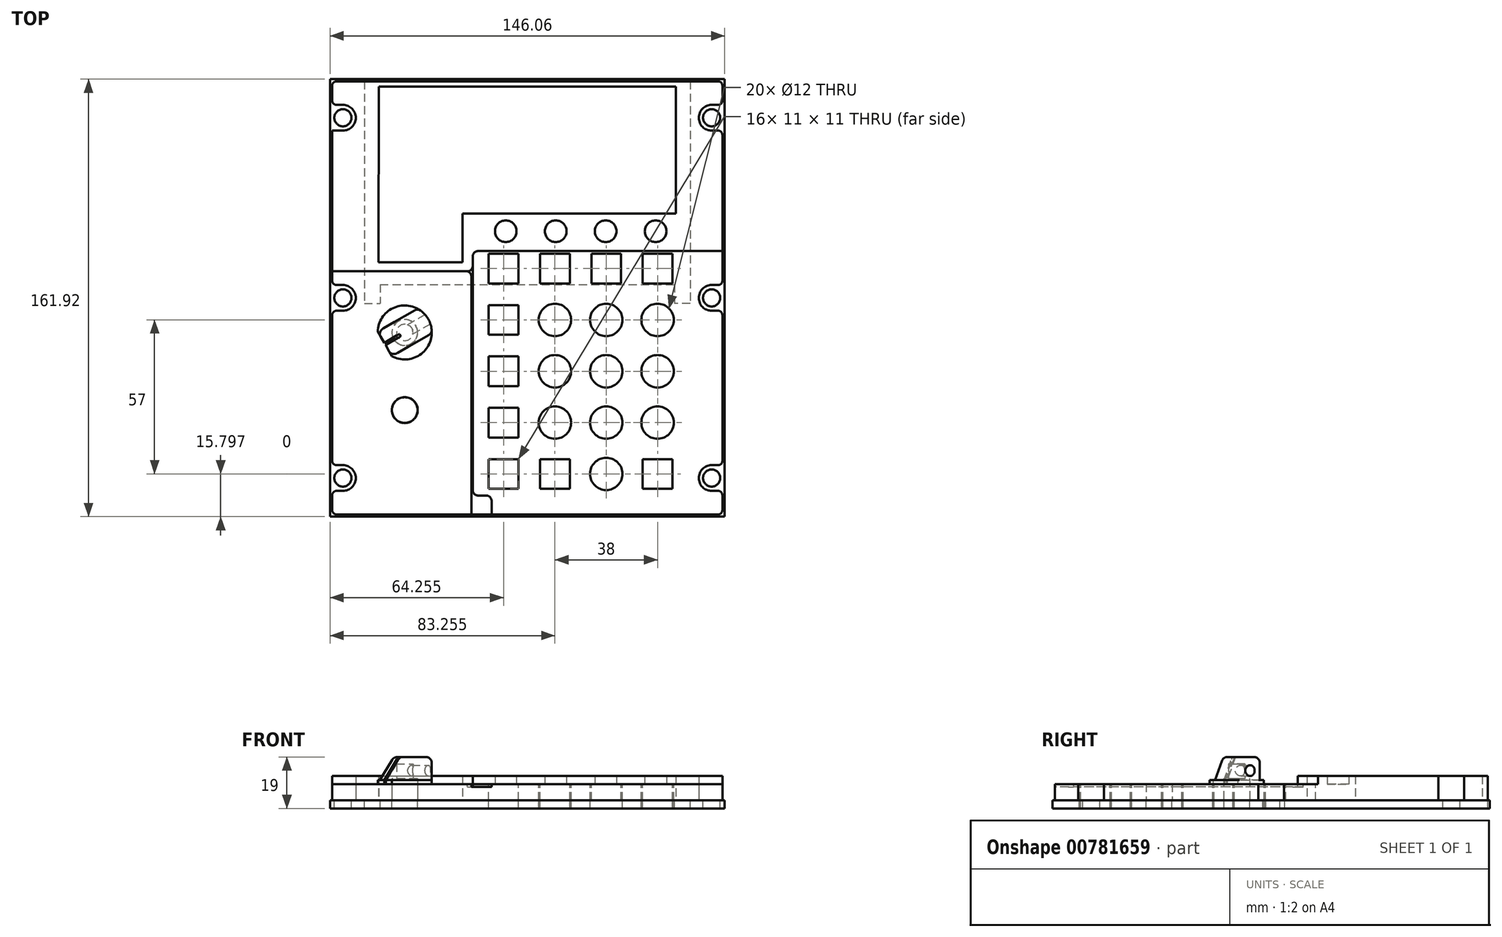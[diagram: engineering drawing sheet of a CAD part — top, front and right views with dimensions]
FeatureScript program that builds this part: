
annotation { "Feature Type Name" : "Feature", "Feature Type Description" : "" }
export const myFeature = defineFeature(function(context is Context, id is Id, definition is map)
    precondition{}
    {
        {
            var Q0;
            Q0=qCreatedBy(makeId("Top.planeOp"),FACE);
            var sketch = newSketch(context, id + "F0", { "sketchPlane" : qUnion([Q0])});
            skLineSegment(sketch, "E0.bottom", {"start": v(73.03, 80.96) * mm, "end": v(-73.03, 80.96) * mm});
            skLineSegment(sketch, "E0.top", {"start": v(73.02, -80.96) * mm, "end": v(-73.02, -80.96) * mm});
            skLineSegment(sketch, "E0.left", {"start": v(73.02, 80.96) * mm, "end": v(73.03, -80.96) * mm});
            skLineSegment(sketch, "E0.right", {"start": v(-73.03, 80.96) * mm, "end": v(-73.03, -80.96) * mm});
            skPoint(sketch, "E0.middle", {"position": v(0, 0) * mm});
            skLineSegment(sketch, "E1.bottom", {"start": v(-72.23, 80.16) * mm, "end": v(72.22, 80.16) * mm});
            skLineSegment(sketch, "E1.top", {"start": v(-72.23, -80.16) * mm, "end": v(72.22, -80.16) * mm});
            skLineSegment(sketch, "E1.left", {"start": v(-72.22, 80.16) * mm, "end": v(-72.22, 71.44) * mm});
            skLineSegment(sketch, "E1.right", {"start": v(72.23, 80.16) * mm, "end": v(72.23, 71.44) * mm});
            skCircle(sketch, "E2", {"center": v(-68.26, 66.67) * mm, "radius": 3.17 * mm});
            skArc(sketch, "E3", {"start": v(-68.26, 61.91) * mm, "mid": v(-63.5, 66.67) * mm, "end": v(-68.26, 71.44) * mm});
            skLineSegment(sketch, "E4", {"start": v(-68.26, 71.44) * mm, "end": v(-72.22, 71.44) * mm});
            skLineSegment(sketch, "E5", {"start": v(-68.26, 61.91) * mm, "end": v(-72.22, 61.91) * mm});
            skArc(sketch, "E6", {"start": v(-68.26, -4.76) * mm, "mid": v(-63.5, 0) * mm, "end": v(-68.26, 4.76) * mm});
            skCircle(sketch, "E7", {"center": v(-68.26, 0) * mm, "radius": 3.17 * mm});
            skLineSegment(sketch, "E8", {"start": v(-68.26, 4.76) * mm, "end": v(-72.23, 4.76) * mm});
            skLineSegment(sketch, "E9", {"start": v(-68.26, -4.76) * mm, "end": v(-72.23, -4.76) * mm});
            skLineSegment(sketch, "E10.trimOffspring", {"start": v(-72.23, -4.76) * mm, "end": v(-72.23, -61.91) * mm});
            skLineSegment(sketch, "E11.trimOffspring", {"start": v(-72.22, 61.91) * mm, "end": v(-72.23, 4.76) * mm});
            skLineSegment(sketch, "E12.MirrorCS", {"start": v(-68.26, -71.44) * mm, "end": v(-72.22, -71.44) * mm});
            skLineSegment(sketch, "E13.MirrorCS", {"start": v(-68.26, -61.91) * mm, "end": v(-72.22, -61.91) * mm});
            skCircle(sketch, "E14.MirrorC", {"center": v(-68.26, -66.67) * mm, "radius": 3.17 * mm});
            skArc(sketch, "E15.MirrorCS", {"start": v(-68.26, -61.91) * mm, "mid": v(-63.5, -66.67) * mm, "end": v(-68.26, -71.44) * mm});
            skCircle(sketch, "E16.MirrorC", {"center": v(68.26, 66.67) * mm, "radius": 3.17 * mm});
            skLineSegment(sketch, "E17.MirrorCS", {"start": v(68.26, 71.44) * mm, "end": v(72.22, 71.44) * mm});
            skLineSegment(sketch, "E18.MirrorCS", {"start": v(68.26, 4.76) * mm, "end": v(72.23, 4.76) * mm});
            skLineSegment(sketch, "E19.MirrorCS", {"start": v(68.26, 61.91) * mm, "end": v(72.22, 61.91) * mm});
            skLineSegment(sketch, "E20.MirrorCS", {"start": v(68.26, -4.76) * mm, "end": v(72.23, -4.76) * mm});
            skCircle(sketch, "E21.MirrorC", {"center": v(68.26, -66.67) * mm, "radius": 3.17 * mm});
            skCircle(sketch, "E22.MirrorC", {"center": v(68.26, 0) * mm, "radius": 3.17 * mm});
            skLineSegment(sketch, "E23.MirrorCS", {"start": v(68.26, -61.91) * mm, "end": v(72.22, -61.91) * mm});
            skArc(sketch, "E24.MirrorCS", {"start": v(68.26, 61.91) * mm, "mid": v(63.5, 66.67) * mm, "end": v(68.26, 71.44) * mm});
            skArc(sketch, "E25.MirrorCS", {"start": v(68.26, -4.76) * mm, "mid": v(63.5, 0) * mm, "end": v(68.26, 4.76) * mm});
            skArc(sketch, "E26.MirrorCS", {"start": v(68.26, -61.91) * mm, "mid": v(63.5, -66.67) * mm, "end": v(68.26, -71.44) * mm});
            skLineSegment(sketch, "E27.MirrorCS", {"start": v(68.26, -71.44) * mm, "end": v(72.22, -71.44) * mm});
            skLineSegment(sketch, "E28", {"start": v(-55.1, 13.16) * mm, "end": v(-23.98, 13.16) * mm});
            skLineSegment(sketch, "E29", {"start": v(-23.98, 13.16) * mm, "end": v(-23.98, 31.16) * mm});
            skLineSegment(sketch, "E30", {"start": v(-23.98, 31.16) * mm, "end": v(55, 31.16) * mm});
            skLineSegment(sketch, "E31", {"start": v(55, 31.16) * mm, "end": v(55, 78.16) * mm});
            skLineSegment(sketch, "E32", {"start": v(55, 78.16) * mm, "end": v(-55, 78.16) * mm});
            skLineSegment(sketch, "E33", {"start": v(-55, 78.16) * mm, "end": v(-55.1, 13.16) * mm});
            skPoint(sketch, "E34", {"position": v(-68.26, 14.26) * mm});
            skPoint(sketch, "E35", {"position": v(-68.26, 56.91) * mm});
            skPoint(sketch, "E36.MirrorP", {"position": v(-68.26, -14.26) * mm});
            skPoint(sketch, "E37.MirrorP", {"position": v(-68.26, -56.91) * mm});
            skPoint(sketch, "E38.MirrorP", {"position": v(68.26, 14.26) * mm});
            skPoint(sketch, "E39.MirrorP", {"position": v(68.26, -14.26) * mm});
            skPoint(sketch, "E40.MirrorP", {"position": v(68.26, -56.91) * mm});
            skPoint(sketch, "E41.MirrorP", {"position": v(68.26, 56.91) * mm});
            skPoint(sketch, "E42", {"position": v(-45.37, -12.8) * mm});
            skPoint(sketch, "E43", {"position": v(-45.37, -41.53) * mm});
            skPoint(sketch, "E44", {"position": v(-45.37, -66.67) * mm});
            skLineSegment(sketch, "E45.trimOffspring", {"start": v(-72.23, -71.44) * mm, "end": v(-72.23, -80.16) * mm});
            skLineSegment(sketch, "E46.trimOffspring", {"start": v(72.22, -71.44) * mm, "end": v(72.22, -80.16) * mm});
            skLineSegment(sketch, "E47.trimOffspring", {"start": v(72.23, -4.76) * mm, "end": v(72.22, -61.91) * mm});
            skLineSegment(sketch, "E48.trimOffspring", {"start": v(72.23, 61.91) * mm, "end": v(72.23, 4.76) * mm});
            skSolve(sketch);
        }
        {
            var Q0;
            Q0=makeQuery(id+"F0.imprint","IMPRINT",FACE,{"disambiguationData":[TD([[makeQuery(id+"F0.imprint","IMPRINT",EDGE,{"derivedFrom":sQuery(id+"F0.wireOp",EDGE,"E0.bottom")}),1.0]])]});
            var Q1;
            {var subQ8=sQuery(id+"F0.wireOp",EDGE,"E1.bottom");Q1=makeQuery(id+"F0.imprint","IMPRINT",FACE,{"disambiguationData":[TD([[makeQuery(id+"F0.imprint","IMPRINT",EDGE,{"derivedFrom":subQ8}),-1.0]])]});}
            var Q2;
            Q2=makeQuery(id+"F0.imprint","IMPRINT",FACE,{"disambiguationData":[TD([[makeQuery(id+"F0.imprint","IMPRINT",EDGE,{"derivedFrom":sQuery(id+"F0.wireOp",EDGE,"E28")}),1.0]])]});
            extrude(context, id + "F1", {"entities" : qUnion([Q0, Q1, Q2]), "oppositeDirection" : true, "depth" : 3 * mm, "offsetDistance" : 25 * mm});
        }
        {
            var Q0;
            Q0=makeQuery(id+"F0.imprint","IMPRINT",FACE,{"disambiguationData":[TD([[makeQuery(id+"F0.imprint","IMPRINT",EDGE,{"derivedFrom":sQuery(id+"F0.wireOp",EDGE,"E1.bottom")}),-1.0]])]});
            extrude(context, id + "F2", {"entities" : qUnion([Q0]), "depth" : 6 * mm, "offsetDistance" : 25 * mm});
        }
        {
            var Q0;
            Q0=makeQuery(id+"F2.opExtrude","SWEPT_EDGE",EDGE,{"disambiguationData":[OSD([sQuery(id+"F0.wireOp",EDGE,"E1.top"),sQuery(id+"F0.wireOp",EDGE,"E45.trimOffspring")])]});
            var Q1;
            Q1=makeQuery(id+"F2.opExtrude","SWEPT_EDGE",EDGE,{"disambiguationData":[OSD([sQuery(id+"F0.wireOp",EDGE,"E10.trimOffspring"),sQuery(id+"F0.wireOp",EDGE,"E13.MirrorCS")])]});
            var Q2;
            Q2=makeQuery(id+"F2.opExtrude","SWEPT_EDGE",EDGE,{"disambiguationData":[OSD([sQuery(id+"F0.wireOp",EDGE,"E12.MirrorCS"),sQuery(id+"F0.wireOp",EDGE,"E45.trimOffspring")])]});
            var Q3;
            Q3=makeQuery(id+"F2.opExtrude","SWEPT_EDGE",EDGE,{"disambiguationData":[OSD([sQuery(id+"F0.wireOp",EDGE,"E9"),sQuery(id+"F0.wireOp",EDGE,"E10.trimOffspring")])]});
            var Q4;
            Q4=makeQuery(id+"F2.opExtrude","SWEPT_EDGE",EDGE,{"disambiguationData":[OSD([sQuery(id+"F0.wireOp",EDGE,"E8"),sQuery(id+"F0.wireOp",EDGE,"E11.trimOffspring")])]});
            var Q5;
            Q5=makeQuery(id+"F2.opExtrude","SWEPT_EDGE",EDGE,{"disambiguationData":[OSD([sQuery(id+"F0.wireOp",EDGE,"E1.bottom"),sQuery(id+"F0.wireOp",EDGE,"E1.left")])]});
            var Q6;
            Q6=makeQuery(id+"F2.opExtrude","SWEPT_EDGE",EDGE,{"disambiguationData":[OSD([sQuery(id+"F0.wireOp",EDGE,"E1.left"),sQuery(id+"F0.wireOp",EDGE,"E4")])]});
            var Q7;
            Q7=makeQuery(id+"F2.opExtrude","SWEPT_EDGE",EDGE,{"disambiguationData":[OSD([sQuery(id+"F0.wireOp",EDGE,"E1.top"),sQuery(id+"F0.wireOp",EDGE,"E46.trimOffspring")])]});
            var Q8;
            Q8=makeQuery(id+"F2.opExtrude","SWEPT_EDGE",EDGE,{"disambiguationData":[OSD([sQuery(id+"F0.wireOp",EDGE,"E27.MirrorCS"),sQuery(id+"F0.wireOp",EDGE,"E46.trimOffspring")])]});
            var Q9;
            Q9=makeQuery(id+"F2.opExtrude","SWEPT_EDGE",EDGE,{"disambiguationData":[OSD([sQuery(id+"F0.wireOp",EDGE,"E23.MirrorCS"),sQuery(id+"F0.wireOp",EDGE,"E47.trimOffspring")])]});
            var Q10;
            Q10=makeQuery(id+"F2.opExtrude","SWEPT_EDGE",EDGE,{"disambiguationData":[OSD([sQuery(id+"F0.wireOp",EDGE,"E20.MirrorCS"),sQuery(id+"F0.wireOp",EDGE,"E47.trimOffspring")])]});
            var Q11;
            Q11=makeQuery(id+"F2.opExtrude","SWEPT_EDGE",EDGE,{"disambiguationData":[OSD([sQuery(id+"F0.wireOp",EDGE,"E18.MirrorCS"),sQuery(id+"F0.wireOp",EDGE,"E48.trimOffspring")])]});
            var Q12;
            Q12=makeQuery(id+"F2.opExtrude","SWEPT_EDGE",EDGE,{"disambiguationData":[OSD([sQuery(id+"F0.wireOp",EDGE,"E1.right"),sQuery(id+"F0.wireOp",EDGE,"E17.MirrorCS")])]});
            var Q13;
            Q13=makeQuery(id+"F2.opExtrude","SWEPT_EDGE",EDGE,{"disambiguationData":[OSD([sQuery(id+"F0.wireOp",EDGE,"E19.MirrorCS"),sQuery(id+"F0.wireOp",EDGE,"E48.trimOffspring")])]});
            var Q14;
            Q14=makeQuery(id+"F2.opExtrude","SWEPT_EDGE",EDGE,{"disambiguationData":[OSD([sQuery(id+"F0.wireOp",EDGE,"E1.bottom"),sQuery(id+"F0.wireOp",EDGE,"E1.right")])]});
            fillet(context, id + "F3", {"entities" : qUnion([Q0, Q1, Q2, Q3, Q4, Q5, Q6, Q7, Q8, Q9, Q10, Q11, Q12, Q13, Q14]), "radius" : 1.59 * mm, "tangentPropagation" : true, "allowEdgeOverflow" : false});
        }
        {
            var Q0;
            Q0=makeQuery(id+"F0.imprint","IMPRINT",FACE,{"disambiguationData":[TD([[makeQuery(id+"F0.imprint","IMPRINT",EDGE,{"derivedFrom":sQuery(id+"F0.wireOp",EDGE,"E1.bottom")}),-1.0]])]});
            var sketch = newSketch(context, id + "F4", { "sketchPlane" : qUnion([Q0])});
            skLineSegment(sketch, "E49.bottom", {"start": v(54, 77.6) * mm, "end": v(-54, 77.6) * mm});
            skLineSegment(sketch, "E49.top", {"start": v(54, 12.8) * mm, "end": v(-54, 12.8) * mm});
            skLineSegment(sketch, "E49.left", {"start": v(54, 77.6) * mm, "end": v(54, 12.8) * mm});
            skLineSegment(sketch, "E49.right", {"start": v(-54, 77.6) * mm, "end": v(-54, 12.8) * mm});
            skPoint(sketch, "E49.middle", {"position": v(0, 42.96) * mm});
            skLineSegment(sketch, "E50.bottom", {"start": v(-60.35, 80.96) * mm, "end": v(60.35, 80.96) * mm});
            skLineSegment(sketch, "E50.top", {"start": v(-54.5, 4.96) * mm, "end": v(54.5, 4.96) * mm});
            skLineSegment(sketch, "E50.left", {"start": v(-60.35, 80.96) * mm, "end": v(-60.35, 4.96) * mm});
            skLineSegment(sketch, "E50.right", {"start": v(60.35, 80.96) * mm, "end": v(60.35, 4.96) * mm});
            skLineSegment(sketch, "E51.top", {"start": v(-60.35, -2.04) * mm, "end": v(-54.5, -2.04) * mm});
            skLineSegment(sketch, "E51.left", {"start": v(-60.35, 4.96) * mm, "end": v(-60.35, -2.04) * mm});
            skLineSegment(sketch, "E51.right", {"start": v(-54.5, 4.96) * mm, "end": v(-54.5, -2.04) * mm});
            skLineSegment(sketch, "E52.MirrorCS", {"start": v(60.35, 4.96) * mm, "end": v(60.35, -2.04) * mm});
            skLineSegment(sketch, "E53.MirrorCS", {"start": v(60.35, -2.04) * mm, "end": v(54.5, -2.04) * mm});
            skLineSegment(sketch, "E54.MirrorCS", {"start": v(54.5, 4.96) * mm, "end": v(54.5, -2.04) * mm});
            skLineSegment(sketch, "E55", {"start": v(-54.5, 4.96) * mm, "end": v(-60.35, 4.96) * mm});
            skLineSegment(sketch, "E56", {"start": v(54.5, 4.96) * mm, "end": v(60.35, 4.96) * mm});
            skSolve(sketch);
        }
        {
            var Q0;
            Q0=makeQuery(id+"F2.opExtrude","CAP_FACE",FACE,{"disambiguationData":[OSD([sQuery(id+"F0.wireOp",EDGE,"E1.bottom"),sQuery(id+"F0.wireOp",EDGE,"E1.top"),sQuery(id+"F0.wireOp",EDGE,"E1.left"),sQuery(id+"F0.wireOp",EDGE,"E1.right"),sQuery(id+"F0.wireOp",EDGE,"E3"),sQuery(id+"F0.wireOp",EDGE,"E4"),sQuery(id+"F0.wireOp",EDGE,"E5"),sQuery(id+"F0.wireOp",EDGE,"E6"),sQuery(id+"F0.wireOp",EDGE,"E8"),sQuery(id+"F0.wireOp",EDGE,"E9"),sQuery(id+"F0.wireOp",EDGE,"E10.trimOffspring"),sQuery(id+"F0.wireOp",EDGE,"E11.trimOffspring"),sQuery(id+"F0.wireOp",EDGE,"E12.MirrorCS"),sQuery(id+"F0.wireOp",EDGE,"E13.MirrorCS"),sQuery(id+"F0.wireOp",EDGE,"E15.MirrorCS"),sQuery(id+"F0.wireOp",EDGE,"E17.MirrorCS"),sQuery(id+"F0.wireOp",EDGE,"E18.MirrorCS"),sQuery(id+"F0.wireOp",EDGE,"E19.MirrorCS"),sQuery(id+"F0.wireOp",EDGE,"E20.MirrorCS"),sQuery(id+"F0.wireOp",EDGE,"E23.MirrorCS"),sQuery(id+"F0.wireOp",EDGE,"E24.MirrorCS"),sQuery(id+"F0.wireOp",EDGE,"E25.MirrorCS"),sQuery(id+"F0.wireOp",EDGE,"E26.MirrorCS"),sQuery(id+"F0.wireOp",EDGE,"E27.MirrorCS"),sQuery(id+"F0.wireOp",EDGE,"E28"),sQuery(id+"F0.wireOp",EDGE,"E29"),sQuery(id+"F0.wireOp",EDGE,"E30"),sQuery(id+"F0.wireOp",EDGE,"E31"),sQuery(id+"F0.wireOp",EDGE,"E32"),sQuery(id+"F0.wireOp",EDGE,"E33"),sQuery(id+"F0.wireOp",EDGE,"E45.trimOffspring"),sQuery(id+"F0.wireOp",EDGE,"E46.trimOffspring"),sQuery(id+"F0.wireOp",EDGE,"E47.trimOffspring"),sQuery(id+"F0.wireOp",EDGE,"E48.trimOffspring")])],"isStart":false});
            var sketch = newSketch(context, id + "F5", { "sketchPlane" : qUnion([Q0])});
            skCircle(sketch, "E57", {"center": v(10.23, -8.16) * mm, "radius": 6 * mm});
            skCircle(sketch, "E58.0.1.0", {"center": v(10.23, -27.16) * mm, "radius": 6 * mm});
            skCircle(sketch, "E58.0.2.0", {"center": v(10.23, -46.16) * mm, "radius": 6 * mm});
            skCircle(sketch, "E58.1.0.0", {"center": v(29.23, -8.16) * mm, "radius": 6 * mm});
            skCircle(sketch, "E58.1.1.0", {"center": v(29.23, -27.16) * mm, "radius": 6 * mm});
            skCircle(sketch, "E58.1.2.0", {"center": v(29.23, -46.16) * mm, "radius": 6 * mm});
            skCircle(sketch, "E58.2.0.0", {"center": v(48.23, -8.16) * mm, "radius": 6 * mm});
            skCircle(sketch, "E58.2.1.0", {"center": v(48.23, -27.16) * mm, "radius": 6 * mm});
            skCircle(sketch, "E58.2.2.0", {"center": v(48.23, -46.16) * mm, "radius": 6 * mm});
            skLineSegment(sketch, "E58.direction1", {"start": v(10.23, -8.16) * mm, "end": v(29.23, -8.16) * mm, "construction": true});
            skLineSegment(sketch, "E58.direction2", {"start": v(10.23, -8.16) * mm, "end": v(10.23, -27.16) * mm, "construction": true});
            skCircle(sketch, "E59", {"center": v(29.23, -65.16) * mm, "radius": 6 * mm});
            skLineSegment(sketch, "E60.bottom", {"start": v(15.73, 16.34) * mm, "end": v(4.73, 16.34) * mm});
            skLineSegment(sketch, "E60.top", {"start": v(15.73, 5.34) * mm, "end": v(4.73, 5.34) * mm});
            skLineSegment(sketch, "E60.left", {"start": v(15.73, 16.34) * mm, "end": v(15.73, 5.34) * mm});
            skLineSegment(sketch, "E60.right", {"start": v(4.73, 16.34) * mm, "end": v(4.73, 5.34) * mm});
            skPoint(sketch, "E60.middle", {"position": v(10.23, 10.84) * mm});
            skLineSegment(sketch, "E61.1.0.0", {"start": v(34.73, 16.34) * mm, "end": v(23.73, 16.34) * mm});
            skLineSegment(sketch, "E61.1.0.1", {"start": v(34.73, 5.34) * mm, "end": v(23.73, 5.34) * mm});
            skLineSegment(sketch, "E61.1.0.2", {"start": v(34.73, 16.34) * mm, "end": v(34.73, 5.34) * mm});
            skLineSegment(sketch, "E61.1.0.3", {"start": v(23.73, 16.34) * mm, "end": v(23.73, 5.34) * mm});
            skPoint(sketch, "E61.1.0.4", {"position": v(29.23, 10.84) * mm});
            skLineSegment(sketch, "E61.2.0.0", {"start": v(53.73, 16.34) * mm, "end": v(42.73, 16.34) * mm});
            skLineSegment(sketch, "E61.2.0.1", {"start": v(53.73, 5.34) * mm, "end": v(42.73, 5.34) * mm});
            skLineSegment(sketch, "E61.2.0.2", {"start": v(53.73, 16.34) * mm, "end": v(53.73, 5.34) * mm});
            skLineSegment(sketch, "E61.2.0.3", {"start": v(42.73, 16.34) * mm, "end": v(42.73, 5.34) * mm});
            skPoint(sketch, "E61.2.0.4", {"position": v(48.23, 10.84) * mm});
            skLineSegment(sketch, "E61.direction1", {"start": v(4.73, 5.34) * mm, "end": v(23.73, 5.34) * mm, "construction": true});
            skLineSegment(sketch, "E62.bottom", {"start": v(-3.27, 16.34) * mm, "end": v(-14.27, 16.34) * mm});
            skLineSegment(sketch, "E62.top", {"start": v(-3.27, 5.34) * mm, "end": v(-14.27, 5.34) * mm});
            skLineSegment(sketch, "E62.left", {"start": v(-3.27, 16.34) * mm, "end": v(-3.27, 5.34) * mm});
            skLineSegment(sketch, "E62.right", {"start": v(-14.27, 16.34) * mm, "end": v(-14.27, 5.34) * mm});
            skPoint(sketch, "E62.middle", {"position": v(-8.77, 10.84) * mm});
            skLineSegment(sketch, "E63.bottom", {"start": v(-3.27, -2.66) * mm, "end": v(-14.27, -2.66) * mm});
            skLineSegment(sketch, "E63.top", {"start": v(-3.27, -13.66) * mm, "end": v(-14.27, -13.66) * mm});
            skLineSegment(sketch, "E63.left", {"start": v(-3.27, -2.66) * mm, "end": v(-3.27, -13.66) * mm});
            skLineSegment(sketch, "E63.right", {"start": v(-14.27, -2.66) * mm, "end": v(-14.27, -13.66) * mm});
            skPoint(sketch, "E63.middle", {"position": v(-8.77, -8.16) * mm});
            skPoint(sketch, "E63.middle.positionSnap0", {"position": v(-8.77, 5.34) * mm});
            skPoint(sketch, "E63.centerSnap0", {"position": v(-8.77, 5.34) * mm});
            skLineSegment(sketch, "E64.bottom", {"start": v(-3.27, -21.66) * mm, "end": v(-14.28, -21.66) * mm});
            skLineSegment(sketch, "E64.top", {"start": v(-3.27, -32.66) * mm, "end": v(-14.27, -32.66) * mm});
            skLineSegment(sketch, "E64.left", {"start": v(-3.27, -21.66) * mm, "end": v(-3.27, -32.66) * mm});
            skLineSegment(sketch, "E64.right", {"start": v(-14.27, -21.66) * mm, "end": v(-14.27, -32.66) * mm});
            skPoint(sketch, "E64.middle", {"position": v(-8.77, -27.16) * mm});
            skLineSegment(sketch, "E65.bottom", {"start": v(-3.27, -40.66) * mm, "end": v(-14.27, -40.66) * mm});
            skLineSegment(sketch, "E65.top", {"start": v(-3.27, -51.66) * mm, "end": v(-14.27, -51.66) * mm});
            skLineSegment(sketch, "E65.left", {"start": v(-3.27, -40.66) * mm, "end": v(-3.27, -51.66) * mm});
            skLineSegment(sketch, "E65.right", {"start": v(-14.27, -40.66) * mm, "end": v(-14.27, -51.66) * mm});
            skPoint(sketch, "E65.middle", {"position": v(-8.77, -46.16) * mm});
            skLineSegment(sketch, "E66.bottom", {"start": v(-3.27, -59.66) * mm, "end": v(-14.27, -59.66) * mm});
            skLineSegment(sketch, "E66.top", {"start": v(-3.27, -70.66) * mm, "end": v(-14.27, -70.66) * mm});
            skLineSegment(sketch, "E66.left", {"start": v(-3.27, -59.66) * mm, "end": v(-3.27, -70.66) * mm});
            skLineSegment(sketch, "E66.right", {"start": v(-14.27, -59.66) * mm, "end": v(-14.27, -70.66) * mm});
            skPoint(sketch, "E66.middle", {"position": v(-8.77, -65.16) * mm});
            skLineSegment(sketch, "E67.bottom", {"start": v(15.73, -59.66) * mm, "end": v(4.73, -59.66) * mm});
            skLineSegment(sketch, "E67.top", {"start": v(15.73, -70.66) * mm, "end": v(4.73, -70.66) * mm});
            skLineSegment(sketch, "E67.left", {"start": v(15.73, -59.66) * mm, "end": v(15.73, -70.66) * mm});
            skLineSegment(sketch, "E67.right", {"start": v(4.73, -59.66) * mm, "end": v(4.73, -70.66) * mm});
            skPoint(sketch, "E67.middle", {"position": v(10.23, -65.16) * mm});
            skLineSegment(sketch, "E68.bottom", {"start": v(53.72, -59.66) * mm, "end": v(42.73, -59.66) * mm});
            skLineSegment(sketch, "E68.top", {"start": v(53.72, -70.66) * mm, "end": v(42.73, -70.66) * mm});
            skLineSegment(sketch, "E68.left", {"start": v(53.72, -59.66) * mm, "end": v(53.72, -70.66) * mm});
            skLineSegment(sketch, "E68.right", {"start": v(42.73, -59.66) * mm, "end": v(42.73, -70.66) * mm});
            skPoint(sketch, "E68.middle", {"position": v(48.23, -65.16) * mm});
            skSolve(sketch);
        }
        {
            var Q0;
            Q0 = qSketchRegion(id + "F5", true);
            extrude(context, id + "F6", {"entities" : qUnion([Q0]), "operationType" : NewBodyOperationType.REMOVE, "oppositeDirection" : true, "depth" : 25 * mm, "offsetDistance" : 25 * mm});
        }
        {
            var Q0;
            Q0=sQuery(id+"F0.wireOp",VERTEX,"E42");
            var Q1;
            Q1=sQuery(id+"F0.wireOp",VERTEX,"E43");
            var Q2;
            Q2=makeQuery(id+"F1.opExtrude","SWEPT_BODY",BODY,{"disambiguationData":[OSD([sQuery(id+"F0.wireOp",EDGE,"E0.bottom"),sQuery(id+"F0.wireOp",EDGE,"E0.top"),sQuery(id+"F0.wireOp",EDGE,"E0.left"),sQuery(id+"F0.wireOp",EDGE,"E0.right"),sQuery(id+"F0.wireOp",EDGE,"E2"),sQuery(id+"F0.wireOp",EDGE,"E7"),sQuery(id+"F0.wireOp",EDGE,"E14.MirrorC"),sQuery(id+"F0.wireOp",EDGE,"E16.MirrorC"),sQuery(id+"F0.wireOp",EDGE,"E21.MirrorC"),sQuery(id+"F0.wireOp",EDGE,"E22.MirrorC")])]});
            hole(context, id + "F7", {"style" : HoleStyle.SIMPLE, "endStyle" : HoleEndStyle.BLIND, "holeDiameter" : 9.5 * mm, "majorDiameter" : 5 * mm, "holeDepth" : 25 * mm, "isTappedThrough" : true, "tappedDepth" : 12 * mm, "tapClearance" : 3, "locations" : qUnion([Q0, Q1]), "scope" : qUnion([Q2])});
        }
        {
            var Q0;
            Q0=sQuery(id+"F0.wireOp",VERTEX,"E42");
            var Q1;
            Q1=sQuery(id+"F0.wireOp",VERTEX,"E43");
            var Q2;
            Q2=makeQuery(id+"F2.opExtrude","SWEPT_BODY",BODY,{"disambiguationData":[OSD([sQuery(id+"F0.wireOp",EDGE,"E1.bottom"),sQuery(id+"F0.wireOp",EDGE,"E1.top"),sQuery(id+"F0.wireOp",EDGE,"E1.left"),sQuery(id+"F0.wireOp",EDGE,"E1.right"),sQuery(id+"F0.wireOp",EDGE,"E3"),sQuery(id+"F0.wireOp",EDGE,"E4"),sQuery(id+"F0.wireOp",EDGE,"E5"),sQuery(id+"F0.wireOp",EDGE,"E6"),sQuery(id+"F0.wireOp",EDGE,"E8"),sQuery(id+"F0.wireOp",EDGE,"E9"),sQuery(id+"F0.wireOp",EDGE,"E10.trimOffspring"),sQuery(id+"F0.wireOp",EDGE,"E11.trimOffspring"),sQuery(id+"F0.wireOp",EDGE,"E12.MirrorCS"),sQuery(id+"F0.wireOp",EDGE,"E13.MirrorCS"),sQuery(id+"F0.wireOp",EDGE,"E15.MirrorCS"),sQuery(id+"F0.wireOp",EDGE,"E17.MirrorCS"),sQuery(id+"F0.wireOp",EDGE,"E18.MirrorCS"),sQuery(id+"F0.wireOp",EDGE,"E19.MirrorCS"),sQuery(id+"F0.wireOp",EDGE,"E20.MirrorCS"),sQuery(id+"F0.wireOp",EDGE,"E23.MirrorCS"),sQuery(id+"F0.wireOp",EDGE,"E24.MirrorCS"),sQuery(id+"F0.wireOp",EDGE,"E25.MirrorCS"),sQuery(id+"F0.wireOp",EDGE,"E26.MirrorCS"),sQuery(id+"F0.wireOp",EDGE,"E27.MirrorCS"),sQuery(id+"F0.wireOp",EDGE,"E28"),sQuery(id+"F0.wireOp",EDGE,"E29"),sQuery(id+"F0.wireOp",EDGE,"E30"),sQuery(id+"F0.wireOp",EDGE,"E31"),sQuery(id+"F0.wireOp",EDGE,"E32"),sQuery(id+"F0.wireOp",EDGE,"E33"),sQuery(id+"F0.wireOp",EDGE,"E45.trimOffspring"),sQuery(id+"F0.wireOp",EDGE,"E46.trimOffspring"),sQuery(id+"F0.wireOp",EDGE,"E47.trimOffspring"),sQuery(id+"F0.wireOp",EDGE,"E48.trimOffspring")])]});
            hole(context, id + "F8", {"style" : HoleStyle.SIMPLE, "endStyle" : HoleEndStyle.BLIND, "oppositeDirection" : true, "holeDiameter" : 9.6 * mm, "majorDiameter" : 5 * mm, "holeDepth" : 25 * mm, "isTappedThrough" : true, "tappedDepth" : 12 * mm, "tapClearance" : 3, "locations" : qUnion([Q0, Q1]), "scope" : qUnion([Q2])});
        }
        {
            var Q0;
            Q0=makeQuery(id+"F2.opExtrude","CAP_FACE",FACE,{"disambiguationData":[OSD([sQuery(id+"F0.wireOp",EDGE,"E1.bottom"),sQuery(id+"F0.wireOp",EDGE,"E1.top"),sQuery(id+"F0.wireOp",EDGE,"E1.left"),sQuery(id+"F0.wireOp",EDGE,"E1.right"),sQuery(id+"F0.wireOp",EDGE,"E3"),sQuery(id+"F0.wireOp",EDGE,"E4"),sQuery(id+"F0.wireOp",EDGE,"E5"),sQuery(id+"F0.wireOp",EDGE,"E6"),sQuery(id+"F0.wireOp",EDGE,"E8"),sQuery(id+"F0.wireOp",EDGE,"E9"),sQuery(id+"F0.wireOp",EDGE,"E10.trimOffspring"),sQuery(id+"F0.wireOp",EDGE,"E11.trimOffspring"),sQuery(id+"F0.wireOp",EDGE,"E12.MirrorCS"),sQuery(id+"F0.wireOp",EDGE,"E13.MirrorCS"),sQuery(id+"F0.wireOp",EDGE,"E15.MirrorCS"),sQuery(id+"F0.wireOp",EDGE,"E17.MirrorCS"),sQuery(id+"F0.wireOp",EDGE,"E18.MirrorCS"),sQuery(id+"F0.wireOp",EDGE,"E19.MirrorCS"),sQuery(id+"F0.wireOp",EDGE,"E20.MirrorCS"),sQuery(id+"F0.wireOp",EDGE,"E23.MirrorCS"),sQuery(id+"F0.wireOp",EDGE,"E24.MirrorCS"),sQuery(id+"F0.wireOp",EDGE,"E25.MirrorCS"),sQuery(id+"F0.wireOp",EDGE,"E26.MirrorCS"),sQuery(id+"F0.wireOp",EDGE,"E27.MirrorCS"),sQuery(id+"F0.wireOp",EDGE,"E28"),sQuery(id+"F0.wireOp",EDGE,"E29"),sQuery(id+"F0.wireOp",EDGE,"E30"),sQuery(id+"F0.wireOp",EDGE,"E31"),sQuery(id+"F0.wireOp",EDGE,"E32"),sQuery(id+"F0.wireOp",EDGE,"E33"),sQuery(id+"F0.wireOp",EDGE,"E45.trimOffspring"),sQuery(id+"F0.wireOp",EDGE,"E46.trimOffspring"),sQuery(id+"F0.wireOp",EDGE,"E47.trimOffspring"),sQuery(id+"F0.wireOp",EDGE,"E48.trimOffspring")])],"isStart":false});
            var sketch = newSketch(context, id + "F9", { "sketchPlane" : qUnion([Q0])});
            skArc(sketch, "E69", {"start": v(-50.1, -21.6) * mm, "mid": v(-36.71, -7.8) * mm, "end": v(-55.37, -12.49) * mm});
            skLineSegment(sketch, "E70", {"start": v(-50.1, -21.6) * mm, "end": v(-55.37, -12.49) * mm});
            skLineSegment(sketch, "E71", {"start": v(-55.37, -12.49) * mm, "end": v(-40.65, -3.99) * mm});
            skLineSegment(sketch, "E72", {"start": v(-50.1, -21.6) * mm, "end": v(-35.38, -13.1) * mm});
            skLineSegment(sketch, "E73", {"start": v(-44.9, -18.6) * mm, "end": v(-50.17, -9.49) * mm});
            skSolve(sketch);
        }
        {
            var Q0;
            {var subQ5=sQuery(id+"F9.wireOp",EDGE,"E69");var subQ7=sQuery(id+"F9.wireOp",EDGE,"E71");var subQ8=makeQuery(id+"F9.imprint","INTERSECT",VERTEX,{"derivedFrom":[subQ5,subQ7]});Q0=makeQuery(id+"F9.imprint","IMPRINT",FACE,{"disambiguationData":[TD([[makeQuery(id+"F9.imprint","IMPRINT",EDGE,{"disambiguationData":[TD([[subQ8,1.0]])],"derivedFrom":subQ5}),1.0]])]});}
            var Q1;
            {var subQ0=sQuery(id+"F9.wireOp",EDGE,"E73");var subQ1=makeQuery(id+"F8.hole-0.boolean.opBoolean","INTERSECT",EDGE,{"derivedFrom":[makeQuery(id+"F2.opExtrude","CAP_FACE",FACE,{"disambiguationData":[OSD([sQuery(id+"F0.wireOp",EDGE,"E1.bottom"),sQuery(id+"F0.wireOp",EDGE,"E1.top"),sQuery(id+"F0.wireOp",EDGE,"E1.left"),sQuery(id+"F0.wireOp",EDGE,"E1.right"),sQuery(id+"F0.wireOp",EDGE,"E3"),sQuery(id+"F0.wireOp",EDGE,"E4"),sQuery(id+"F0.wireOp",EDGE,"E5"),sQuery(id+"F0.wireOp",EDGE,"E6"),sQuery(id+"F0.wireOp",EDGE,"E8"),sQuery(id+"F0.wireOp",EDGE,"E9"),sQuery(id+"F0.wireOp",EDGE,"E10.trimOffspring"),sQuery(id+"F0.wireOp",EDGE,"E11.trimOffspring"),sQuery(id+"F0.wireOp",EDGE,"E12.MirrorCS"),sQuery(id+"F0.wireOp",EDGE,"E13.MirrorCS"),sQuery(id+"F0.wireOp",EDGE,"E15.MirrorCS"),sQuery(id+"F0.wireOp",EDGE,"E17.MirrorCS"),sQuery(id+"F0.wireOp",EDGE,"E18.MirrorCS"),sQuery(id+"F0.wireOp",EDGE,"E19.MirrorCS"),sQuery(id+"F0.wireOp",EDGE,"E20.MirrorCS"),sQuery(id+"F0.wireOp",EDGE,"E23.MirrorCS"),sQuery(id+"F0.wireOp",EDGE,"E24.MirrorCS"),sQuery(id+"F0.wireOp",EDGE,"E25.MirrorCS"),sQuery(id+"F0.wireOp",EDGE,"E26.MirrorCS"),sQuery(id+"F0.wireOp",EDGE,"E27.MirrorCS"),sQuery(id+"F0.wireOp",EDGE,"E28"),sQuery(id+"F0.wireOp",EDGE,"E29"),sQuery(id+"F0.wireOp",EDGE,"E30"),sQuery(id+"F0.wireOp",EDGE,"E31"),sQuery(id+"F0.wireOp",EDGE,"E32"),sQuery(id+"F0.wireOp",EDGE,"E33"),sQuery(id+"F0.wireOp",EDGE,"E45.trimOffspring"),sQuery(id+"F0.wireOp",EDGE,"E46.trimOffspring"),sQuery(id+"F0.wireOp",EDGE,"E47.trimOffspring"),sQuery(id+"F0.wireOp",EDGE,"E48.trimOffspring")])],"isStart":false}),makeQuery(id+"F8.hole-0.opRevolve","SWEPT_FACE",FACE,{"disambiguationData":[OSD([sQuery(id+"F8.hole-0.sketch.wireOp",EDGE,"core_line_2")])]})]});var subQ2=makeQuery(id+"F9.imprint","INTERSECT",VERTEX,{"disambiguationData":[OD(0.0)],"derivedFrom":[subQ1,subQ0]});Q1=makeQuery(id+"F9.imprint","IMPRINT",FACE,{"disambiguationData":[TD([[makeQuery(id+"F9.imprint","IMPRINT",EDGE,{"disambiguationData":[TD([[subQ2,-1.0]])],"derivedFrom":subQ0}),-1.0]])]});}
            var Q2;
            {var subQ1=sQuery(id+"F9.wireOp",EDGE,"E70");Q2=makeQuery(id+"F9.imprint","IMPRINT",FACE,{"disambiguationData":[TD([[makeQuery(id+"F9.imprint","IMPRINT",EDGE,{"derivedFrom":subQ1}),-1.0]])]});}
            var Q3;
            {var subQ0=sQuery(id+"F9.wireOp",EDGE,"E73");var subQ1=makeQuery(id+"F8.hole-0.boolean.opBoolean","INTERSECT",EDGE,{"derivedFrom":[makeQuery(id+"F2.opExtrude","CAP_FACE",FACE,{"disambiguationData":[OSD([sQuery(id+"F0.wireOp",EDGE,"E1.bottom"),sQuery(id+"F0.wireOp",EDGE,"E1.top"),sQuery(id+"F0.wireOp",EDGE,"E1.left"),sQuery(id+"F0.wireOp",EDGE,"E1.right"),sQuery(id+"F0.wireOp",EDGE,"E3"),sQuery(id+"F0.wireOp",EDGE,"E4"),sQuery(id+"F0.wireOp",EDGE,"E5"),sQuery(id+"F0.wireOp",EDGE,"E6"),sQuery(id+"F0.wireOp",EDGE,"E8"),sQuery(id+"F0.wireOp",EDGE,"E9"),sQuery(id+"F0.wireOp",EDGE,"E10.trimOffspring"),sQuery(id+"F0.wireOp",EDGE,"E11.trimOffspring"),sQuery(id+"F0.wireOp",EDGE,"E12.MirrorCS"),sQuery(id+"F0.wireOp",EDGE,"E13.MirrorCS"),sQuery(id+"F0.wireOp",EDGE,"E15.MirrorCS"),sQuery(id+"F0.wireOp",EDGE,"E17.MirrorCS"),sQuery(id+"F0.wireOp",EDGE,"E18.MirrorCS"),sQuery(id+"F0.wireOp",EDGE,"E19.MirrorCS"),sQuery(id+"F0.wireOp",EDGE,"E20.MirrorCS"),sQuery(id+"F0.wireOp",EDGE,"E23.MirrorCS"),sQuery(id+"F0.wireOp",EDGE,"E24.MirrorCS"),sQuery(id+"F0.wireOp",EDGE,"E25.MirrorCS"),sQuery(id+"F0.wireOp",EDGE,"E26.MirrorCS"),sQuery(id+"F0.wireOp",EDGE,"E27.MirrorCS"),sQuery(id+"F0.wireOp",EDGE,"E28"),sQuery(id+"F0.wireOp",EDGE,"E29"),sQuery(id+"F0.wireOp",EDGE,"E30"),sQuery(id+"F0.wireOp",EDGE,"E31"),sQuery(id+"F0.wireOp",EDGE,"E32"),sQuery(id+"F0.wireOp",EDGE,"E33"),sQuery(id+"F0.wireOp",EDGE,"E45.trimOffspring"),sQuery(id+"F0.wireOp",EDGE,"E46.trimOffspring"),sQuery(id+"F0.wireOp",EDGE,"E47.trimOffspring"),sQuery(id+"F0.wireOp",EDGE,"E48.trimOffspring")])],"isStart":false}),makeQuery(id+"F8.hole-0.opRevolve","SWEPT_FACE",FACE,{"disambiguationData":[OSD([sQuery(id+"F8.hole-0.sketch.wireOp",EDGE,"core_line_2")])]})]});var subQ2=makeQuery(id+"F9.imprint","INTERSECT",VERTEX,{"disambiguationData":[OD(0.0)],"derivedFrom":[subQ1,subQ0]});Q3=makeQuery(id+"F9.imprint","IMPRINT",FACE,{"disambiguationData":[TD([[makeQuery(id+"F9.imprint","IMPRINT",EDGE,{"disambiguationData":[TD([[subQ2,-1.0]])],"derivedFrom":subQ0}),1.0]])]});}
            extrude(context, id + "F10", {"entities" : qUnion([Q0, Q1, Q2, Q3]), "depth" : 10 * mm, "offsetDistance" : 25 * mm});
        }
        {
            var Q0;
            {var subQ0=sQuery(id+"F9.wireOp",EDGE,"E72");var subQ1=sQuery(id+"F9.wireOp",EDGE,"E69");var subQ3=makeQuery(id+"F9.imprint","INTERSECT",VERTEX,{"derivedFrom":[subQ1,subQ0]});Q0=makeQuery(id+"F9.imprint","IMPRINT",FACE,{"disambiguationData":[TD([[makeQuery(id+"F9.imprint","IMPRINT",EDGE,{"disambiguationData":[TD([[subQ3,1.0]])],"derivedFrom":subQ0}),-1.0]])]});}
            var Q1;
            {var subQ0=sQuery(id+"F9.wireOp",EDGE,"E71");var subQ1=sQuery(id+"F9.wireOp",EDGE,"E69");var subQ3=makeQuery(id+"F9.imprint","INTERSECT",VERTEX,{"derivedFrom":[subQ1,subQ0]});Q1=makeQuery(id+"F9.imprint","IMPRINT",FACE,{"disambiguationData":[TD([[makeQuery(id+"F9.imprint","IMPRINT",EDGE,{"disambiguationData":[TD([[subQ3,1.0]])],"derivedFrom":subQ0}),1.0]])]});}
            extrude(context, id + "F11", {"entities" : qUnion([Q0, Q1]), "operationType" : NewBodyOperationType.ADD, "depth" : 1.5 * mm, "offsetDistance" : 25 * mm});
        }
        {
            var Q0;
            Q0=makeQuery(id+"F10.opExtrude","CAP_EDGE",EDGE,{"disambiguationData":[OSD([sQuery(id+"F9.wireOp",EDGE,"E70")])],"isStart":false});
            chamfer(context, id + "F12", {"entities" : qUnion([Q0]), "chamferType" : ChamferType.TWO_OFFSETS, "width1" : 6 * mm, "oppositeDirection" : true, "width2" : 8.5 * mm, "tangentPropagation" : true});
        }
        {
            var Q0;
            Q0=makeQuery(id+"F12.opChamfer","BLEND_FACE",FACE,{"disambiguationData":[OSD([sQuery(id+"F9.wireOp",EDGE,"E70")])]});
            var sketch = newSketch(context, id + "F13", { "sketchPlane" : qUnion([Q0])});
            skLineSegment(sketch, "E74", {"start": v(-6.36, -17.63) * mm, "end": v(-3.07, -27.5) * mm});
            skLineSegment(sketch, "E75", {"start": v(-2.6, -27.35) * mm, "end": v(-5.89, -17.48) * mm});
            skLineSegment(sketch, "E76", {"start": v(-6.83, -17.8) * mm, "end": v(-3.55, -27.66) * mm});
            skLineSegment(sketch, "E77", {"start": v(-5.89, -17.48) * mm, "end": v(-6.16, -16.66) * mm});
            skLineSegment(sketch, "E78", {"start": v(-6.16, -16.66) * mm, "end": v(-7.1, -16.97) * mm});
            skLineSegment(sketch, "E79", {"start": v(-6.83, -17.8) * mm, "end": v(-7.1, -16.97) * mm});
            skLineSegment(sketch, "E80", {"start": v(-7.1, -16.97) * mm, "end": v(-7.1, -16.97) * mm});
            skPoint(sketch, "E81.orphan", {"position": v(-7.11, -16.97) * mm});
            skSolve(sketch);
        }
        {
            var Q0;
            {var subQ0=sQuery(id+"F13.wireOp",EDGE,"E74");Q0=makeQuery(id+"F13.imprint","IMPRINT",FACE,{"disambiguationData":[TD([[makeQuery(id+"F13.imprint","IMPRINT",EDGE,{"derivedFrom":subQ0}),-1.0]])]});}
            var Q1;
            {var subQ0=sQuery(id+"F13.wireOp",EDGE,"E74");Q1=makeQuery(id+"F13.imprint","IMPRINT",FACE,{"disambiguationData":[TD([[makeQuery(id+"F13.imprint","IMPRINT",EDGE,{"derivedFrom":subQ0}),1.0]])]});}
            var Q2;
            {var subQ4=sQuery(id+"F13.wireOp",EDGE,"E77");Q2=makeQuery(id+"F13.imprint","IMPRINT",FACE,{"disambiguationData":[TD([[makeQuery(id+"F13.imprint","IMPRINT",EDGE,{"derivedFrom":subQ4}),1.0]])]});}
            var Q3;
            {var subQ4=sQuery(id+"F13.wireOp",EDGE,"T1NhCv4N-vA1D-NOaW-mEF3-bBURzNNSlZRk");Q3=makeQuery(id+"F13.imprint","IMPRINT",FACE,{"disambiguationData":[TD([[makeQuery(id+"F13.imprint","IMPRINT",EDGE,{"derivedFrom":subQ4}),1.0]])]});}
            extrude(context, id + "F14", {"entities" : qUnion([Q0, Q1, Q2, Q3]), "operationType" : NewBodyOperationType.REMOVE, "oppositeDirection" : true, "depth" : .5 * mm, "offsetDistance" : 25 * mm});
        }
        {
            var Q0;
            {var subQ0=sQuery(id+"F9.wireOp",EDGE,"E70");var subQ1=sQuery(id+"F9.wireOp",EDGE,"E71");var subQ2=sQuery(id+"F9.wireOp",EDGE,"E72");var subQ3=sQuery(id+"F9.wireOp",EDGE,"E69");var subQ4=makeQuery(id+"F10.opExtrude","CAP_FACE",FACE,{"disambiguationData":[OSD([subQ3,subQ0,subQ1,subQ2])],"isStart":false});Q0=makeQuery(id+"F14.boolean.opBoolean","SPLIT",EDGE,{"disambiguationData":[TD([makeQuery(id+"F10.opExtrude","SWEPT_FACE",FACE,{"disambiguationData":[OSD([subQ1])]})])],"derivedFrom":makeQuery(id+"F12.opChamfer","BLEND_EDGE",EDGE,{"blendedFrom":[makeQuery(id+"F10.opExtrude","CAP_EDGE",EDGE,{"disambiguationData":[OSD([subQ0])],"isStart":false}),subQ4],"blendedInto":[subQ4]})});}
            var Q1;
            Q1=makeQuery(id+"F10.opExtrude","CAP_EDGE",EDGE,{"disambiguationData":[OSD([sQuery(id+"F9.wireOp",EDGE,"E72")])],"isStart":false});
            var Q2;
            Q2=makeQuery(id+"F12.opChamfer","BLEND_EDGE",EDGE,{"blendedFrom":[makeQuery(id+"F10.opExtrude","CAP_EDGE",EDGE,{"disambiguationData":[OSD([sQuery(id+"F9.wireOp",EDGE,"E70")])],"isStart":false}),makeQuery(id+"F10.opExtrude","SWEPT_FACE",FACE,{"disambiguationData":[OSD([sQuery(id+"F9.wireOp",EDGE,"E72")])]})],"blendedInto":[makeQuery(id+"F10.opExtrude","SWEPT_FACE",FACE,{"disambiguationData":[OSD([sQuery(id+"F9.wireOp",EDGE,"E72")])]})]});
            var Q3;
            Q3=makeQuery(id+"F12.opChamfer","BLEND_EDGE",EDGE,{"blendedFrom":[makeQuery(id+"F10.opExtrude","CAP_EDGE",EDGE,{"disambiguationData":[OSD([sQuery(id+"F9.wireOp",EDGE,"E70")])],"isStart":false}),makeQuery(id+"F10.opExtrude","SWEPT_FACE",FACE,{"disambiguationData":[OSD([sQuery(id+"F9.wireOp",EDGE,"E71")])]})],"blendedInto":[makeQuery(id+"F10.opExtrude","SWEPT_FACE",FACE,{"disambiguationData":[OSD([sQuery(id+"F9.wireOp",EDGE,"E71")])]})]});
            var Q4;
            {var subQ0=sQuery(id+"F9.wireOp",EDGE,"E70");var subQ1=sQuery(id+"F9.wireOp",EDGE,"E72");var subQ2=sQuery(id+"F9.wireOp",EDGE,"E71");var subQ3=sQuery(id+"F9.wireOp",EDGE,"E69");var subQ4=makeQuery(id+"F10.opExtrude","CAP_FACE",FACE,{"disambiguationData":[OSD([subQ3,subQ0,subQ2,subQ1])],"isStart":false});Q4=makeQuery(id+"F14.boolean.opBoolean","SPLIT",EDGE,{"disambiguationData":[TD([makeQuery(id+"F10.opExtrude","SWEPT_FACE",FACE,{"disambiguationData":[OSD([subQ1])]})])],"derivedFrom":makeQuery(id+"F12.opChamfer","BLEND_EDGE",EDGE,{"blendedFrom":[makeQuery(id+"F10.opExtrude","CAP_EDGE",EDGE,{"disambiguationData":[OSD([subQ0])],"isStart":false}),subQ4],"blendedInto":[subQ4]})});}
            var Q5;
            Q5=makeQuery(id+"F10.opExtrude","CAP_EDGE",EDGE,{"disambiguationData":[OSD([sQuery(id+"F9.wireOp",EDGE,"E69")])],"isStart":false});
            var Q6;
            Q6=makeQuery(id+"F10.opExtrude","SWEPT_EDGE",EDGE,{"disambiguationData":[OSD([sQuery(id+"F9.wireOp",EDGE,"E69"),sQuery(id+"F9.wireOp",EDGE,"E72")])]});
            var Q7;
            Q7=makeQuery(id+"F10.opExtrude","CAP_EDGE",EDGE,{"disambiguationData":[OSD([sQuery(id+"F9.wireOp",EDGE,"E71")])],"isStart":false});
            var Q8;
            Q8=makeQuery(id+"F10.opExtrude","SWEPT_EDGE",EDGE,{"disambiguationData":[OSD([sQuery(id+"F9.wireOp",EDGE,"E69"),sQuery(id+"F9.wireOp",EDGE,"E71")])]});
            fillet(context, id + "F15", {"entities" : qUnion([Q0, Q1, Q2, Q3, Q4, Q5, Q6, Q7, Q8]), "radius" : 2 * mm, "tangentPropagation" : true, "allowEdgeOverflow" : false});
        }
        {
            var Q0;
            Q0=makeQuery(id+"F10.opExtrude","SWEPT_FACE",FACE,{"disambiguationData":[OSD([sQuery(id+"F9.wireOp",EDGE,"E70")])]});
            var sketch = newSketch(context, id + "F16", { "sketchPlane" : qUnion([Q0])});
            skLineSegment(sketch, "E82", {"start": v(-11.1, 7.5) * mm, "end": v(-11.1, 6) * mm});
            skLineSegment(sketch, "E83", {"start": v(-12.1, 7.5) * mm, "end": v(-12.1, 6) * mm});
            skSolve(sketch);
        }
        {
            var Q0;
            {var subQ0=sQuery(id+"F16.wireOp",EDGE,"E82");Q0=makeQuery(id+"F16.imprint","IMPRINT",FACE,{"disambiguationData":[TD([[makeQuery(id+"F16.imprint","IMPRINT",EDGE,{"derivedFrom":subQ0}),-1.0]])]});}
            extrude(context, id + "F17", {"entities" : qUnion([Q0]), "operationType" : NewBodyOperationType.REMOVE, "oppositeDirection" : true, "depth" : 0.4 * mm, "offsetDistance" : 25 * mm});
        }
        {
            var Q0;
            Q0=makeQuery(id+"F17.boolean.opBoolean","COPY",FACE,{"derivedFrom":makeQuery(id+"F17.opExtrude","CAP_FACE",FACE,{"disambiguationData":[OSD([sQuery(id+"F9.wireOp",EDGE,"E70"),sQuery(id+"F16.wireOp",EDGE,"E82"),sQuery(id+"F16.wireOp",EDGE,"E83")])],"isStart":false})});
            cPlane(context, id + "F18", {"entities" : qUnion([Q0]), "cplaneType" : CPlaneType.OFFSET, "offset" : 20 * mm, "oppositeDirection" : true, "width" : 150 * mm, "height" : 150 * mm});
        }
        {
            var Q0;
            Q0=qCreatedBy(id+"F18.planeOp",FACE);
            var sketch = newSketch(context, id + "F19", { "sketchPlane" : qUnion([Q0])});
            skCircle(sketch, "E84", {"center": v(-11.6, 11) * mm, "radius": 2 * mm});
            skSolve(sketch);
        }
        {
            var Q0;
            {var subQ0=sQuery(id+"F9.wireOp",EDGE,"E71");var subQ1=sQuery(id+"F9.wireOp",EDGE,"E69");var subQ2=sQuery(id+"F9.wireOp",EDGE,"E72");Q0=makeQuery(id+"F11.boolean.opBoolean","MERGE",FACE,{"derivedFrom":[makeQuery(id+"F10.opExtrude","CAP_FACE",FACE,{"disambiguationData":[OSD([subQ1,sQuery(id+"F9.wireOp",EDGE,"E70"),subQ0,subQ2])],"isStart":true}),makeQuery(id+"F11.opExtrude","CAP_FACE",FACE,{"disambiguationData":[OSD([subQ1,subQ2])],"isStart":true}),makeQuery(id+"F11.opExtrude","CAP_FACE",FACE,{"disambiguationData":[OSD([subQ1,subQ0])],"isStart":true})]});}
            var sketch = newSketch(context, id + "F20", { "sketchPlane" : qUnion([Q0])});
            skCircle(sketch, "E85", {"center": v(-45.37, 12.8) * mm, "radius": 4.8 * mm});
            skCircle(sketch, "E86", {"center": v(-45.37, 12.8) * mm, "radius": 3.05 * mm});
            skSolve(sketch);
        }
        {
            var Q0;
            Q0=makeQuery(id+"F20.imprint","IMPRINT",FACE,{"disambiguationData":[TD([[makeQuery(id+"F20.imprint","IMPRINT",EDGE,{"derivedFrom":sQuery(id+"F20.wireOp",EDGE,"E86")}),1.0]])]});
            extrude(context, id + "F21", {"entities" : qUnion([Q0]), "operationType" : NewBodyOperationType.REMOVE, "oppositeDirection" : true, "depth" : 7.5 * mm, "offsetDistance" : 25 * mm});
        }
        {
            var Q0;
            Q0=makeQuery(id+"F20.imprint","IMPRINT",FACE,{"disambiguationData":[TD([[makeQuery(id+"F20.imprint","IMPRINT",EDGE,{"derivedFrom":sQuery(id+"F20.wireOp",EDGE,"E85")}),1.0]])]});
            extrude(context, id + "F22", {"entities" : qUnion([Q0]), "operationType" : NewBodyOperationType.REMOVE, "oppositeDirection" : true, "depth" : 2 * mm, "offsetDistance" : 25 * mm});
        }
        {
            var Q0;
            Q0=makeQuery(id+"F19.imprint","IMPRINT",FACE,{"disambiguationData":[TD([[makeQuery(id+"F19.imprint","IMPRINT",EDGE,{"derivedFrom":sQuery(id+"F19.wireOp",EDGE,"E84")}),1.0]])]});
            extrude(context, id + "F23", {"entities" : qUnion([Q0]), "operationType" : NewBodyOperationType.REMOVE, "depth" : 10 * mm, "offsetDistance" : 25 * mm});
        }
        {
            var Q0;
            Q0=makeQuery(id+"F2.opExtrude","CAP_FACE",FACE,{"disambiguationData":[OSD([sQuery(id+"F0.wireOp",EDGE,"E1.bottom"),sQuery(id+"F0.wireOp",EDGE,"E1.top"),sQuery(id+"F0.wireOp",EDGE,"E1.left"),sQuery(id+"F0.wireOp",EDGE,"E1.right"),sQuery(id+"F0.wireOp",EDGE,"E3"),sQuery(id+"F0.wireOp",EDGE,"E4"),sQuery(id+"F0.wireOp",EDGE,"E5"),sQuery(id+"F0.wireOp",EDGE,"E6"),sQuery(id+"F0.wireOp",EDGE,"E8"),sQuery(id+"F0.wireOp",EDGE,"E9"),sQuery(id+"F0.wireOp",EDGE,"E10.trimOffspring"),sQuery(id+"F0.wireOp",EDGE,"E11.trimOffspring"),sQuery(id+"F0.wireOp",EDGE,"E12.MirrorCS"),sQuery(id+"F0.wireOp",EDGE,"E13.MirrorCS"),sQuery(id+"F0.wireOp",EDGE,"E15.MirrorCS"),sQuery(id+"F0.wireOp",EDGE,"E17.MirrorCS"),sQuery(id+"F0.wireOp",EDGE,"E18.MirrorCS"),sQuery(id+"F0.wireOp",EDGE,"E19.MirrorCS"),sQuery(id+"F0.wireOp",EDGE,"E20.MirrorCS"),sQuery(id+"F0.wireOp",EDGE,"E23.MirrorCS"),sQuery(id+"F0.wireOp",EDGE,"E24.MirrorCS"),sQuery(id+"F0.wireOp",EDGE,"E25.MirrorCS"),sQuery(id+"F0.wireOp",EDGE,"E26.MirrorCS"),sQuery(id+"F0.wireOp",EDGE,"E27.MirrorCS"),sQuery(id+"F0.wireOp",EDGE,"E28"),sQuery(id+"F0.wireOp",EDGE,"E29"),sQuery(id+"F0.wireOp",EDGE,"E30"),sQuery(id+"F0.wireOp",EDGE,"E31"),sQuery(id+"F0.wireOp",EDGE,"E32"),sQuery(id+"F0.wireOp",EDGE,"E33"),sQuery(id+"F0.wireOp",EDGE,"E45.trimOffspring"),sQuery(id+"F0.wireOp",EDGE,"E46.trimOffspring"),sQuery(id+"F0.wireOp",EDGE,"E47.trimOffspring"),sQuery(id+"F0.wireOp",EDGE,"E48.trimOffspring")])],"isStart":false});
            var sketch = newSketch(context, id + "F24", { "sketchPlane" : qUnion([Q0])});
            skLineSegment(sketch, "E87", {"start": v(-72.23, 9.84) * mm, "end": v(-20.23, 9.84) * mm});
            skLineSegment(sketch, "E88", {"start": v(-20.23, 9.84) * mm, "end": v(-20.23, -80.16) * mm});
            skCircle(sketch, "E89", {"center": v(-7.98, 24.66) * mm, "radius": 4 * mm});
            skCircle(sketch, "E90", {"center": v(10.52, 24.66) * mm, "radius": 4 * mm});
            skCircle(sketch, "E91", {"center": v(29.02, 24.66) * mm, "radius": 4 * mm});
            skCircle(sketch, "E92", {"center": v(47.52, 24.66) * mm, "radius": 4 * mm});
            skLineSegment(sketch, "E93", {"start": v(-20.23, 9.84) * mm, "end": v(-20.23, 17.34) * mm});
            skLineSegment(sketch, "E94", {"start": v(-20.23, 17.34) * mm, "end": v(72.23, 17.34) * mm});
            skSolve(sketch);
        }
        {
            var Q0;
            {var subQ20=sQuery(id+"F24.wireOp",EDGE,"E87");Q0=makeQuery(id+"F24.imprint","IMPRINT",FACE,{"disambiguationData":[TD([[makeQuery(id+"F24.imprint","IMPRINT",EDGE,{"derivedFrom":subQ20}),1.0]])]});}
            extrude(context, id + "F25", {"entities" : qUnion([Q0]), "operationType" : NewBodyOperationType.ADD, "depth" : 3 * mm, "offsetDistance" : 25 * mm});
        }
        {
            var Q0;
            Q0=makeQuery(id+"F25.opExtrude","SWEPT_EDGE",EDGE,{"disambiguationData":[OSD([sQuery(id+"F24.wireOp",EDGE,"E93"),sQuery(id+"F24.wireOp",EDGE,"E94")])]});
            var Q1;
            Q1=makeQuery(id+"F25.opExtrude","SWEPT_EDGE",EDGE,{"disambiguationData":[OSD([sQuery(id+"F24.wireOp",EDGE,"E87"),sQuery(id+"F24.wireOp",EDGE,"E88"),sQuery(id+"F24.wireOp",EDGE,"E93")])]});
            fillet(context, id + "F26", {"entities" : qUnion([Q0, Q1]), "radius" : 2 * mm, "tangentPropagation" : true, "allowEdgeOverflow" : false});
        }
        {
            var Q0;
            {var subQ0=sQuery(id+"F0.wireOp",EDGE,"E46.trimOffspring");var subQ1=sQuery(id+"F0.wireOp",EDGE,"E27.MirrorCS");var subQ2=sQuery(id+"F0.wireOp",EDGE,"E20.MirrorCS");var subQ3=sQuery(id+"F0.wireOp",EDGE,"E47.trimOffspring");var subQ4=sQuery(id+"F0.wireOp",EDGE,"E23.MirrorCS");var subQ5=sQuery(id+"F0.wireOp",EDGE,"E18.MirrorCS");var subQ6=sQuery(id+"F0.wireOp",EDGE,"E15.MirrorCS");var subQ7=sQuery(id+"F0.wireOp",EDGE,"E48.trimOffspring");var subQ8=sQuery(id+"F0.wireOp",EDGE,"E13.MirrorCS");var subQ9=sQuery(id+"F0.wireOp",EDGE,"E45.trimOffspring");var subQ10=sQuery(id+"F0.wireOp",EDGE,"E12.MirrorCS");var subQ11=sQuery(id+"F0.wireOp",EDGE,"E11.trimOffspring");var subQ12=sQuery(id+"F0.wireOp",EDGE,"E8");var subQ13=sQuery(id+"F0.wireOp",EDGE,"E10.trimOffspring");var subQ14=sQuery(id+"F0.wireOp",EDGE,"E9");var subQ15=sQuery(id+"F0.wireOp",EDGE,"E1.top");var subQ16=sQuery(id+"F0.wireOp",EDGE,"E6");var subQ17=sQuery(id+"F0.wireOp",EDGE,"E25.MirrorCS");var subQ18=sQuery(id+"F0.wireOp",EDGE,"E26.MirrorCS");Q0=makeQuery(id+"F25.boolean.opBoolean","SPLIT",FACE,{"disambiguationData":[TD([makeQuery(id+"F2.opExtrude","SWEPT_FACE",FACE,{"disambiguationData":[OSD([subQ15])]})])],"derivedFrom":makeQuery(id+"F2.opExtrude","CAP_FACE",FACE,{"disambiguationData":[OSD([sQuery(id+"F0.wireOp",EDGE,"E1.bottom"),subQ15,sQuery(id+"F0.wireOp",EDGE,"E1.left"),sQuery(id+"F0.wireOp",EDGE,"E1.right"),sQuery(id+"F0.wireOp",EDGE,"E3"),sQuery(id+"F0.wireOp",EDGE,"E4"),sQuery(id+"F0.wireOp",EDGE,"E5"),subQ16,subQ12,subQ14,subQ13,subQ11,subQ10,subQ8,subQ6,sQuery(id+"F0.wireOp",EDGE,"E17.MirrorCS"),subQ5,sQuery(id+"F0.wireOp",EDGE,"E19.MirrorCS"),subQ2,subQ4,sQuery(id+"F0.wireOp",EDGE,"E24.MirrorCS"),subQ17,subQ18,subQ1,sQuery(id+"F0.wireOp",EDGE,"E28"),sQuery(id+"F0.wireOp",EDGE,"E29"),sQuery(id+"F0.wireOp",EDGE,"E30"),sQuery(id+"F0.wireOp",EDGE,"E31"),sQuery(id+"F0.wireOp",EDGE,"E32"),sQuery(id+"F0.wireOp",EDGE,"E33"),subQ9,subQ0,subQ3,subQ7])],"isStart":false})});}
            var sketch = newSketch(context, id + "F27", { "sketchPlane" : qUnion([Q0])});
            skLineSegment(sketch, "E95", {"start": v(-20.73, 9.84) * mm, "end": v(-20.73, -80.16) * mm});
            skLineSegment(sketch, "E96", {"start": v(-20.73, 9.84) * mm, "end": v(-22.99, 9.84) * mm});
            skLineSegment(sketch, "E97", {"start": v(-20.23, 9.84) * mm, "end": v(-20.23, -80.16) * mm});
            skLineSegment(sketch, "E98", {"start": v(-20.23, 9.84) * mm, "end": v(-20.23, 11.84) * mm});
            skCircle(sketch, "E99", {"center": v(-17.23, -77.16) * mm, "radius": 2 * mm});
            skLineSegment(sketch, "E100", {"start": v(-20.23, -73.16) * mm, "end": v(-13.23, -73.16) * mm});
            skLineSegment(sketch, "E101", {"start": v(-13.23, -73.16) * mm, "end": v(-13.23, -80.16) * mm});
            skSolve(sketch);
        }
        {
            var Q0;
            {var subQ1=sQuery(id+"F27.wireOp",EDGE,"E95");Q0=makeQuery(id+"F27.imprint","IMPRINT",FACE,{"disambiguationData":[TD([[makeQuery(id+"F27.imprint","IMPRINT",EDGE,{"derivedFrom":subQ1}),1.0]])]});}
            var Q1;
            Q1=makeQuery(id+"F27.imprint","IMPRINT",FACE,{"disambiguationData":[TD([[makeQuery(id+"F27.imprint","IMPRINT",EDGE,{"derivedFrom":sQuery(id+"F27.wireOp",EDGE,"E99")}),-1.0]])]});
            var Q2;
            Q2=makeQuery(id+"F27.imprint","IMPRINT",FACE,{"disambiguationData":[TD([[makeQuery(id+"F27.imprint","IMPRINT",EDGE,{"derivedFrom":sQuery(id+"F27.wireOp",EDGE,"E99")}),1.0]])]});
            extrude(context, id + "F28", {"entities" : qUnion([Q0, Q1, Q2]), "operationType" : NewBodyOperationType.REMOVE, "oppositeDirection" : true, "depth" : 1 * mm, "offsetDistance" : 25 * mm});
        }
        {
            var Q0;
            Q0=makeQuery(id+"F28.boolean.opBoolean","COPY",EDGE,{"derivedFrom":makeQuery(id+"F28.opExtrude","SWEPT_EDGE",EDGE,{"disambiguationData":[OSD([sQuery(id+"F27.wireOp",EDGE,"E95"),sQuery(id+"F27.wireOp",EDGE,"E96")])]})});
            var Q1;
            Q1=makeQuery(id+"F28.boolean.opBoolean","COPY",EDGE,{"derivedFrom":makeQuery(id+"F28.opExtrude","SWEPT_EDGE",EDGE,{"disambiguationData":[OSD([sQuery(id+"F0.wireOp",EDGE,"E1.top"),sQuery(id+"F27.wireOp",EDGE,"E95")])]})});
            var Q2;
            Q2=makeQuery(id+"F28.boolean.opBoolean","COPY",EDGE,{"derivedFrom":makeQuery(id+"F28.opExtrude","SWEPT_EDGE",EDGE,{"disambiguationData":[OSD([sQuery(id+"F27.wireOp",EDGE,"E97"),sQuery(id+"F27.wireOp",EDGE,"E100")])]})});
            var Q3;
            Q3=makeQuery(id+"F28.boolean.opBoolean","COPY",EDGE,{"derivedFrom":makeQuery(id+"F28.opExtrude","SWEPT_EDGE",EDGE,{"disambiguationData":[OSD([sQuery(id+"F27.wireOp",EDGE,"E100"),sQuery(id+"F27.wireOp",EDGE,"E101")])]})});
            var Q4;
            Q4=makeQuery(id+"F28.boolean.opBoolean","COPY",EDGE,{"derivedFrom":makeQuery(id+"F28.opExtrude","SWEPT_EDGE",EDGE,{"disambiguationData":[OSD([sQuery(id+"F0.wireOp",EDGE,"E1.top"),sQuery(id+"F27.wireOp",EDGE,"E101")])]})});
            fillet(context, id + "F29", {"entities" : qUnion([Q0, Q1, Q2, Q3, Q4]), "radius" : 2 * mm, "tangentPropagation" : true, "allowEdgeOverflow" : false});
        }
        {
            var Q0;
            {var subQ9=sQuery(id+"F4.wireOp",EDGE,"E49.top");Q0=makeQuery(id+"F4.imprint","IMPRINT",FACE,{"disambiguationData":[TD([[makeQuery(id+"F4.imprint","IMPRINT",EDGE,{"derivedFrom":subQ9}),1.0]])]});}
            var Q1;
            {var subQ2=sQuery(id+"F4.wireOp",EDGE,"E49.bottom");Q1=makeQuery(id+"F4.imprint","IMPRINT",FACE,{"disambiguationData":[TD([[makeQuery(id+"F4.imprint","IMPRINT",EDGE,{"derivedFrom":subQ2}),1.0]])]});}
            var Q2;
            {var subQ1=sQuery(id+"F4.wireOp",EDGE,"E49.top");Q2=makeQuery(id+"F4.imprint","IMPRINT",FACE,{"disambiguationData":[TD([[makeQuery(id+"F4.imprint","IMPRINT",EDGE,{"derivedFrom":subQ1}),-1.0]])]});}
            var Q3;
            {var subQ1=sQuery(id+"F4.wireOp",EDGE,"E49.bottom");Q3=makeQuery(id+"F4.imprint","IMPRINT",FACE,{"disambiguationData":[TD([[makeQuery(id+"F4.imprint","IMPRINT",EDGE,{"derivedFrom":subQ1}),-1.0]])]});}
            var Q4;
            Q4=makeQuery(id+"F4.imprint","IMPRINT",FACE,{"disambiguationData":[TD([[makeQuery(id+"F4.imprint","IMPRINT",EDGE,{"derivedFrom":sQuery(id+"F4.wireOp",EDGE,"E51.top")}),1.0]])]});
            var Q5;
            Q5=makeQuery(id+"F4.imprint","IMPRINT",FACE,{"disambiguationData":[TD([[makeQuery(id+"F4.imprint","IMPRINT",EDGE,{"derivedFrom":sQuery(id+"F4.wireOp",EDGE,"E52.MirrorCS")}),-1.0]])]});
            extrude(context, id + "F30", {"entities" : qUnion([Q0, Q1, Q2, Q3, Q4, Q5]), "operationType" : NewBodyOperationType.REMOVE, "oppositeDirection" : true, "depth" : 25 * mm, "offsetDistance" : 25 * mm});
        }
    });
